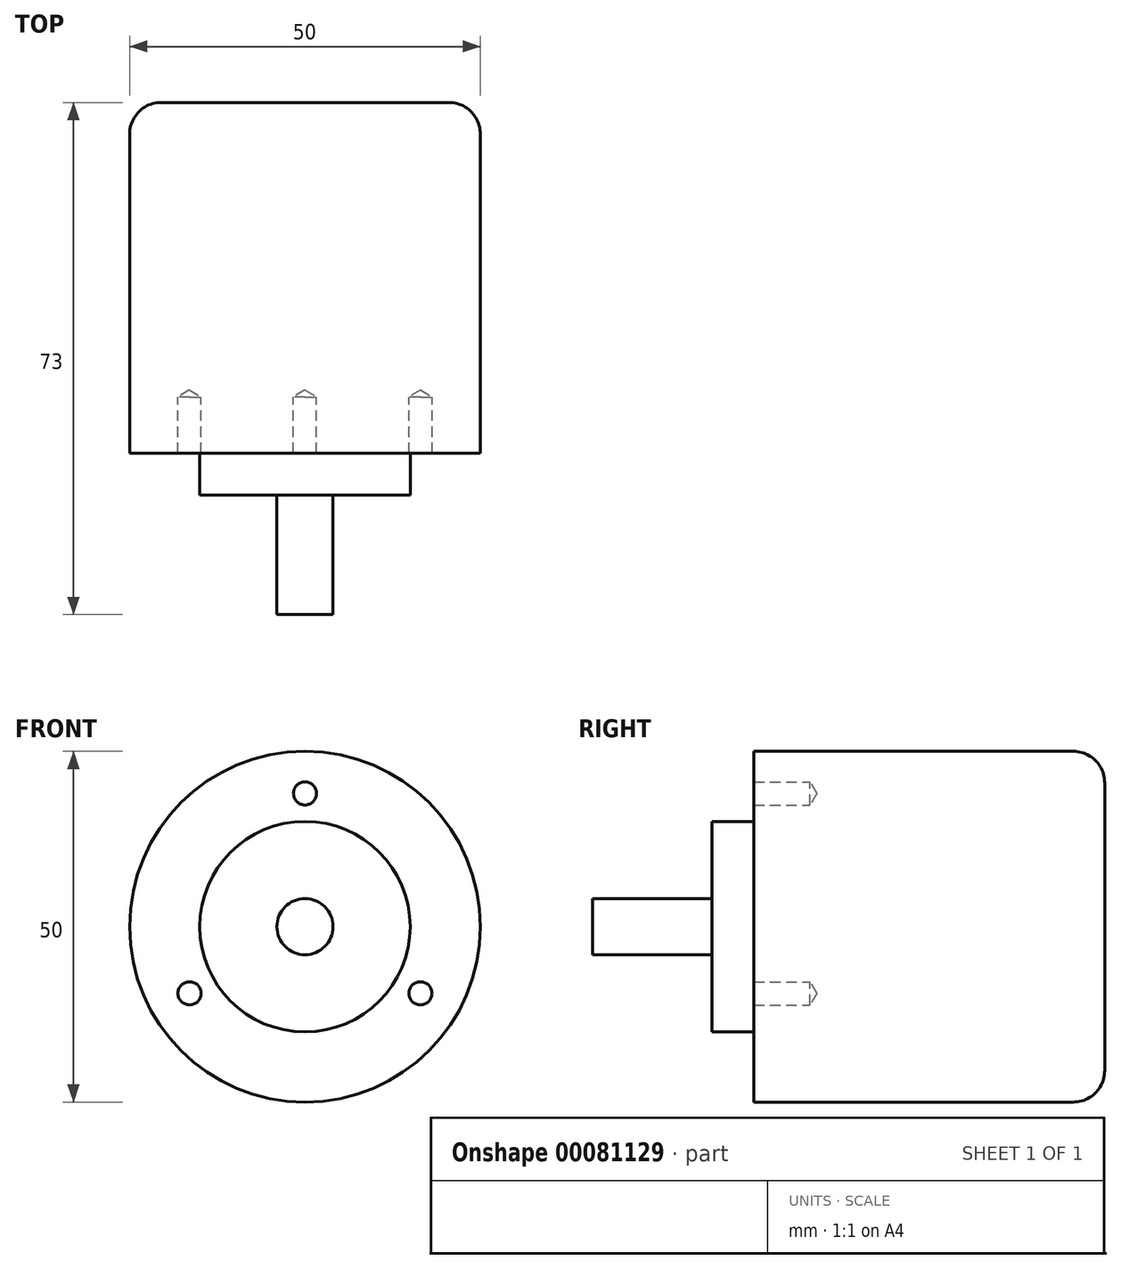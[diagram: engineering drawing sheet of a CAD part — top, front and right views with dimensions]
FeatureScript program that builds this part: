
annotation { "Feature Type Name" : "Feature", "Feature Type Description" : "" }
export const myFeature = defineFeature(function(context is Context, id is Id, definition is map)
    precondition{}
    {
        {
            var Q0;
            Q0=qCreatedBy(makeId("Front.planeOp"),FACE);
            var sketch = newSketch(context, id + "F0", { "sketchPlane" : qUnion([Q0])});
            skCircle(sketch, "E0", {"center": v(0, 0) * mm, "radius": 25 * mm});
            skSolve(sketch);
        }
        {
            var Q0;
            Q0=makeQuery(id+"F0.imprint","IMPRINT",FACE,{"disambiguationData":[TD([[makeQuery(id+"F0.imprint","IMPRINT",EDGE,{"derivedFrom":sQuery(id+"F0.wireOp",EDGE,"E0")}),1.0]])]});
            extrude(context, id + "F1", {"entities" : qUnion([Q0]), "oppositeDirection" : true, "depth" : 50 * mm});
        }
        {
            var Q0;
            Q0=makeQuery(id+"F1.opExtrude","CAP_EDGE",EDGE,{"disambiguationData":[OSD([sQuery(id+"F0.wireOp",EDGE,"E0")])],"isStart":false});
            fillet(context, id + "F2", {"entities" : qUnion([Q0]), "radius" : 4.5 * mm, "tangentPropagation" : true, "allowEdgeOverflow" : false});
        }
        {
            var Q0;
            Q0=makeQuery(id+"F1.opExtrude","CAP_FACE",FACE,{"disambiguationData":[OSD([sQuery(id+"F0.wireOp",EDGE,"E0")])],"isStart":true});
            var sketch = newSketch(context, id + "F3", { "sketchPlane" : qUnion([Q0])});
            skCircle(sketch, "E1", {"center": v(0, 0) * mm, "radius": 15 * mm});
            skCircle(sketch, "E2", {"center": v(0, 0) * mm, "radius": 19 * mm, "construction": true});
            skPoint(sketch, "E3", {"position": v(0, 19) * mm});
            skPoint(sketch, "E4", {"position": v(-16.45, -9.5) * mm});
            skPoint(sketch, "E5", {"position": v(16.45, -9.5) * mm});
            skLineSegment(sketch, "E6", {"start": v(0, 0) * mm, "end": v(-16.45, -9.5) * mm, "construction": true});
            skLineSegment(sketch, "E7", {"start": v(0, 0) * mm, "end": v(16.45, -9.5) * mm, "construction": true});
            skLineSegment(sketch, "E8", {"start": v(0, 0) * mm, "end": v(0, 19) * mm, "construction": true});
            skSolve(sketch);
        }
        {
            var Q0;
            Q0=makeQuery(id+"F3.imprint","IMPRINT",FACE,{"disambiguationData":[TD([[makeQuery(id+"F3.imprint","IMPRINT",EDGE,{"derivedFrom":sQuery(id+"F3.wireOp",EDGE,"E1")}),1.0]])]});
            extrude(context, id + "F4", {"entities" : qUnion([Q0]), "operationType" : NewBodyOperationType.ADD, "depth" : 6 * mm});
        }
        {
            var Q0;
            Q0=sQuery(id+"F3.wireOp",VERTEX,"E3");
            var Q1;
            Q1=sQuery(id+"F3.wireOp",VERTEX,"E4");
            var Q2;
            Q2=sQuery(id+"F3.wireOp",VERTEX,"E5");
            var Q3;
            Q3=makeQuery(id+"F1.opExtrude","SWEPT_BODY",BODY,{"disambiguationData":[OSD([sQuery(id+"F0.wireOp",EDGE,"E0")])]});
            hole(context, id + "F5", {"style" : HoleStyle.SIMPLE, "endStyle" : HoleEndStyle.BLIND, "standardTappedOrClearance" : lookupTablePath({ "standard" : "ISO", "fit" : "Normal", "size" : "M3", "type" : "Clearance" }), "standardBlindInLast" : lookupTablePath({ "fit" : "Standard", "standard" : "ISO", "size" : "M3", "type" : "Clearance" }), "holeDiameter" : 3.3 * mm, "holeDepth" : 8 * mm, "startFromSketch" : true, "locations" : qUnion([Q0, Q1, Q2]), "scope" : qUnion([Q3])});
        }
        {
            var Q0;
            Q0=makeQuery(id+"F4.opExtrude","CAP_FACE",FACE,{"disambiguationData":[OSD([sQuery(id+"F3.wireOp",EDGE,"E1")])],"isStart":false});
            var sketch = newSketch(context, id + "F6", { "sketchPlane" : qUnion([Q0])});
            skCircle(sketch, "E9", {"center": v(0, 0) * mm, "radius": 4 * mm});
            skSolve(sketch);
        }
        {
            var Q0;
            Q0=makeQuery(id+"F6.imprint","IMPRINT",FACE,{"disambiguationData":[TD([[makeQuery(id+"F6.imprint","IMPRINT",EDGE,{"derivedFrom":sQuery(id+"F6.wireOp",EDGE,"E9")}),1.0]])]});
            extrude(context, id + "F7", {"entities" : qUnion([Q0]), "operationType" : NewBodyOperationType.ADD, "depth" : 17 * mm});
        }
    });
